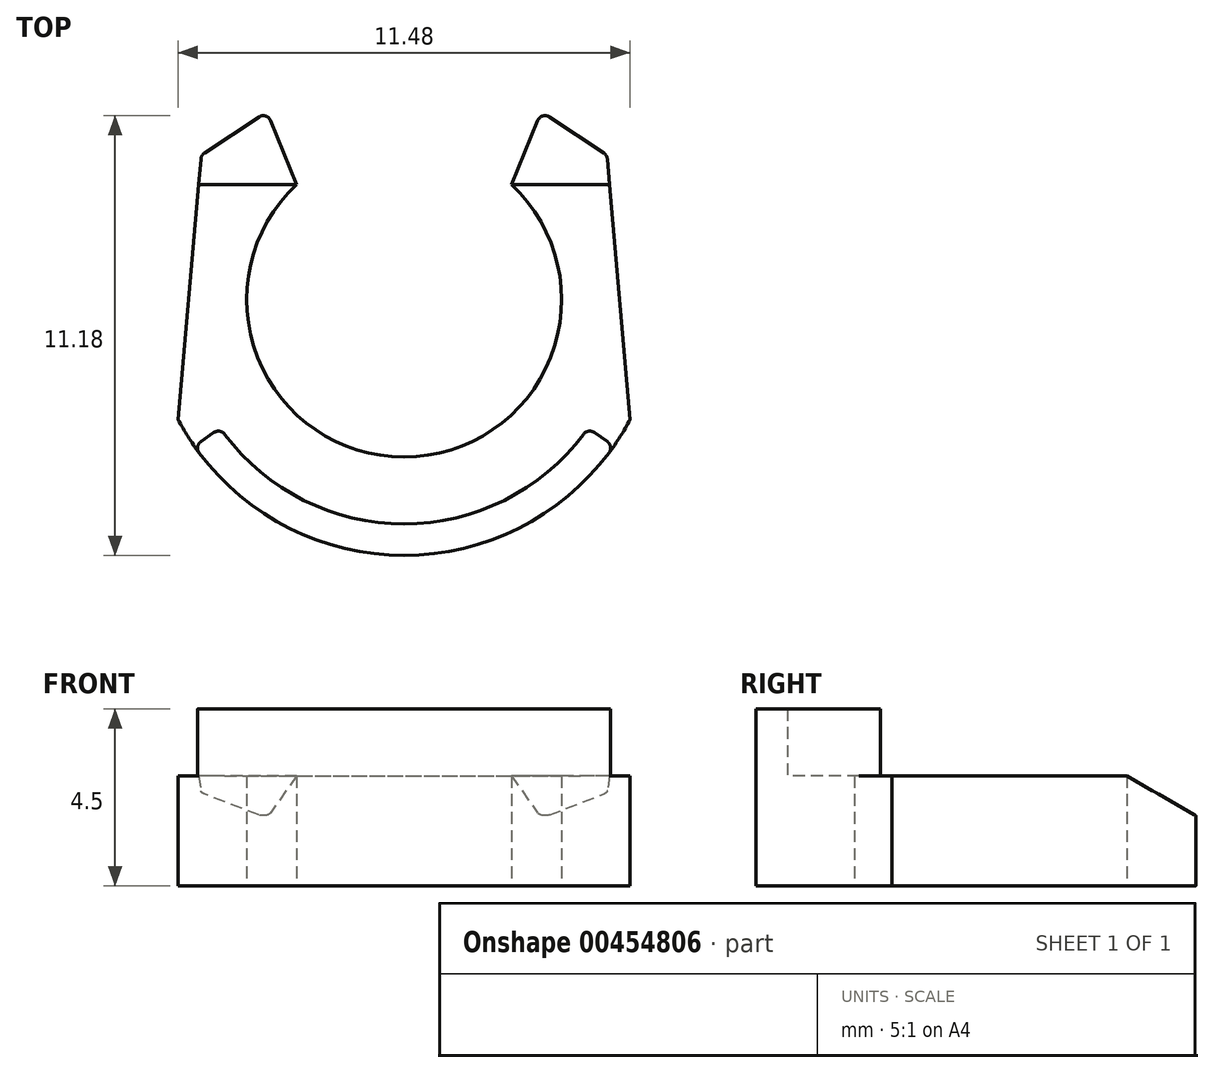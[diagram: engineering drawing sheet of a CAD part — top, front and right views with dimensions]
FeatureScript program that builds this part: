
annotation { "Feature Type Name" : "Feature", "Feature Type Description" : "" }
export const myFeature = defineFeature(function(context is Context, id is Id, definition is map)
    precondition{}
    {
        {
            assignVariable(context, id + "F0", {"name" : "thickness", "anyValue" : 1.3 + 1.5});
        }
        {
            var Q0;
            Q0=qCreatedBy(makeId("Top.planeOp"),FACE);
            var sketch = newSketch(context, id + "F1", { "sketchPlane" : qUnion([Q0])});
            skLineSegment(sketch, "E0.bottom", {"start": v(6, -6) * mm, "end": v(-6, -6) * mm, "construction": true});
            skLineSegment(sketch, "E0.top", {"start": v(4.95, 6) * mm, "end": v(-4.95, 6) * mm, "construction": true});
            skLineSegment(sketch, "E0.left", {"start": v(6, -6) * mm, "end": v(5.74, -3.05) * mm, "construction": true});
            skLineSegment(sketch, "E0.right", {"start": v(-6, -6) * mm, "end": v(-5.74, -3.05) * mm, "construction": true});
            skPoint(sketch, "E0.middle", {"position": v(0, 0) * mm});
            skPoint(sketch, "E1", {"position": v(0, 6) * mm});
            skPoint(sketch, "E2", {"position": v(0, -6) * mm});
            skLineSegment(sketch, "E3", {"start": v(0, 6) * mm, "end": v(0, -6) * mm, "construction": true});
            skLineSegment(sketch, "E4", {"start": v(-5.74, -3.05) * mm, "end": v(-5.15, 3.67) * mm});
            skLineSegment(sketch, "E5", {"start": v(5.74, -3.05) * mm, "end": v(5.15, 3.67) * mm});
            skArc(sketch, "E6", {"start": v(5.74, -3.05) * mm, "mid": v(0, 6.5) * mm, "end": v(-5.74, -3.05) * mm, "construction": true});
            skArc(sketch, "E7", {"start": v(-5.74, -3.05) * mm, "mid": v(0, -6.5) * mm, "end": v(5.74, -3.05) * mm});
            skLineSegment(sketch, "E8", {"start": v(2.73, 2.93) * mm, "end": v(3.49, 4.78) * mm});
            skLineSegment(sketch, "E9", {"start": v(3.49, 4.78) * mm, "end": v(5.15, 3.67) * mm});
            skLineSegment(sketch, "E10", {"start": v(-2.73, 2.93) * mm, "end": v(-3.49, 4.78) * mm});
            skLineSegment(sketch, "E11", {"start": v(-3.49, 4.78) * mm, "end": v(-5.15, 3.67) * mm});
            skLineSegment(sketch, "E12", {"start": v(-5.15, 3.67) * mm, "end": v(-4.95, 6) * mm, "construction": true});
            skLineSegment(sketch, "E13", {"start": v(5.15, 3.67) * mm, "end": v(4.95, 6) * mm, "construction": true});
            skArc(sketch, "E14", {"start": v(2.73, 2.93) * mm, "mid": v(0, 4) * mm, "end": v(-2.73, 2.93) * mm, "construction": true});
            skArc(sketch, "E15", {"start": v(-2.73, 2.93) * mm, "mid": v(0, -4) * mm, "end": v(2.73, 2.93) * mm});
            skSolve(sketch);
        }
        {
            var Q0;
            Q0=qSketchRegion(id+"F1",true);
            extrude(context, id + "F2", {"entities" : qUnion([Q0]), "depth" : (getVariable(context, 'thickness')) * mm});
        }
        {
            var Q0;
            Q0=makeQuery(id+"F2.opExtrude","CAP_FACE",FACE,{"disambiguationData":[OSD([sQuery(id+"F1.wireOp",EDGE,"E4"),sQuery(id+"F1.wireOp",EDGE,"E5"),sQuery(id+"F1.wireOp",EDGE,"E7"),sQuery(id+"F1.wireOp",EDGE,"E8"),sQuery(id+"F1.wireOp",EDGE,"E9"),sQuery(id+"F1.wireOp",EDGE,"E10"),sQuery(id+"F1.wireOp",EDGE,"E11"),sQuery(id+"F1.wireOp",EDGE,"E15")])],"isStart":false});
            var sketch = newSketch(context, id + "F3", { "sketchPlane" : qUnion([Q0])});
            skArc(sketch, "E16.0", {"start": v(-5.33, -3.72) * mm, "mid": v(0, -6.5) * mm, "end": v(5.33, -3.72) * mm});
            skArc(sketch, "E17", {"start": v(-4.67, -3.27) * mm, "mid": v(0, -5.7) * mm, "end": v(4.67, -3.27) * mm});
            skLineSegment(sketch, "E18", {"start": v(0, 0) * mm, "end": v(-4.67, -3.27) * mm, "construction": true});
            skLineSegment(sketch, "E19", {"start": v(-9.02, -6.3) * mm, "end": v(9.02, -6.3) * mm, "construction": true});
            skLineSegment(sketch, "E20", {"start": v(9.02, -6.3) * mm, "end": v(5.33, -3.72) * mm, "construction": true});
            skLineSegment(sketch, "E21", {"start": v(0, -6.3) * mm, "end": v(0, 0) * mm, "construction": true});
            skLineSegment(sketch, "E22", {"start": v(-5.33, -3.72) * mm, "end": v(-9.02, -6.3) * mm});
            skLineSegment(sketch, "E23", {"start": v(-4.67, -3.27) * mm, "end": v(-5.33, -3.72) * mm});
            skLineSegment(sketch, "E24", {"start": v(5.33, -3.72) * mm, "end": v(4.67, -3.27) * mm});
            skLineSegment(sketch, "E25", {"start": v(4.67, -3.27) * mm, "end": v(0, 0) * mm, "construction": true});
            skPoint(sketch, "E26.orphan", {"position": v(-5.74, -3.05) * mm});
            skPoint(sketch, "E27.orphan", {"position": v(5.74, -3.05) * mm});
            skPoint(sketch, "E28", {"position": v(-5, -3.5) * mm});
            skPoint(sketch, "E29", {"position": v(5, -3.5) * mm});
            skSolve(sketch);
        }
        {
            var Q0;
            Q0=qSketchRegion(id+"F3",true);
            extrude(context, id + "F4", {"entities" : qUnion([Q0]), "operationType" : NewBodyOperationType.ADD, "depth" : 1.7 * mm});
        }
        {
            var Q0;
            Q0=qCreatedBy(makeId("Right.planeOp"),FACE);
            var sketch = newSketch(context, id + "F5", { "sketchPlane" : qUnion([Q0])});
            skPoint(sketch, "E30.0", {"position": v(2.93, 2.8) * mm});
            skLineSegment(sketch, "E31", {"start": v(2.93, 2.8) * mm, "end": v(6.78, 0.58) * mm});
            skLineSegment(sketch, "E32", {"start": v(6.78, 0.58) * mm, "end": v(6.78, 2.8) * mm});
            skLineSegment(sketch, "E33", {"start": v(6.78, 2.8) * mm, "end": v(2.93, 2.8) * mm});
            skPoint(sketch, "E34.0", {"position": v(4.78, 2.8) * mm});
            skSolve(sketch);
        }
        {
            var Q0;
            Q0=qSketchRegion(id+"F5",true);
            extrude(context, id + "F6", {"entities" : qUnion([Q0]), "operationType" : NewBodyOperationType.REMOVE, "endBound" : BoundingType.SYMMETRIC, "depth" : 25 * mm});
        }
        {
            var Q0;
            Q0=makeQuery(id+"F4.opExtrude","SWEPT_EDGE",EDGE,{"disambiguationData":[OSD([sQuery(id+"F3.wireOp",EDGE,"E17"),sQuery(id+"F3.wireOp",EDGE,"E24")])]});
            var Q1;
            Q1=makeQuery(id+"F4.opExtrude","SWEPT_EDGE",EDGE,{"disambiguationData":[OSD([sQuery(id+"F1.wireOp",EDGE,"E7"),sQuery(id+"F3.wireOp",EDGE,"E16.0"),sQuery(id+"F3.wireOp",EDGE,"E23")])]});
            var Q2;
            Q2=makeQuery(id+"F4.opExtrude","SWEPT_EDGE",EDGE,{"disambiguationData":[OSD([sQuery(id+"F3.wireOp",EDGE,"E17"),sQuery(id+"F3.wireOp",EDGE,"E23")])]});
            var Q3;
            Q3=makeQuery(id+"F4.opExtrude","SWEPT_EDGE",EDGE,{"disambiguationData":[OSD([sQuery(id+"F1.wireOp",EDGE,"E7"),sQuery(id+"F3.wireOp",EDGE,"E16.0"),sQuery(id+"F3.wireOp",EDGE,"E24")])]});
            var Q4;
            Q4=makeQuery(id+"F2.opExtrude","SWEPT_EDGE",EDGE,{"disambiguationData":[OSD([sQuery(id+"F1.wireOp",EDGE,"E8"),sQuery(id+"F1.wireOp",EDGE,"E9")])]});
            var Q5;
            Q5=makeQuery(id+"F2.opExtrude","SWEPT_EDGE",EDGE,{"disambiguationData":[OSD([sQuery(id+"F1.wireOp",EDGE,"E5"),sQuery(id+"F1.wireOp",EDGE,"E9")])]});
            var Q6;
            Q6=makeQuery(id+"F2.opExtrude","SWEPT_EDGE",EDGE,{"disambiguationData":[OSD([sQuery(id+"F1.wireOp",EDGE,"E10"),sQuery(id+"F1.wireOp",EDGE,"E11")])]});
            var Q7;
            Q7=makeQuery(id+"F2.opExtrude","SWEPT_EDGE",EDGE,{"disambiguationData":[OSD([sQuery(id+"F1.wireOp",EDGE,"E4"),sQuery(id+"F1.wireOp",EDGE,"E11")])]});
            fillet(context, id + "F7", {"entities" : qUnion([Q0, Q1, Q2, Q3, Q4, Q5, Q6, Q7]), "radius" : 0.2 * mm, "tangentPropagation" : true, "allowEdgeOverflow" : false});
        }
    });
